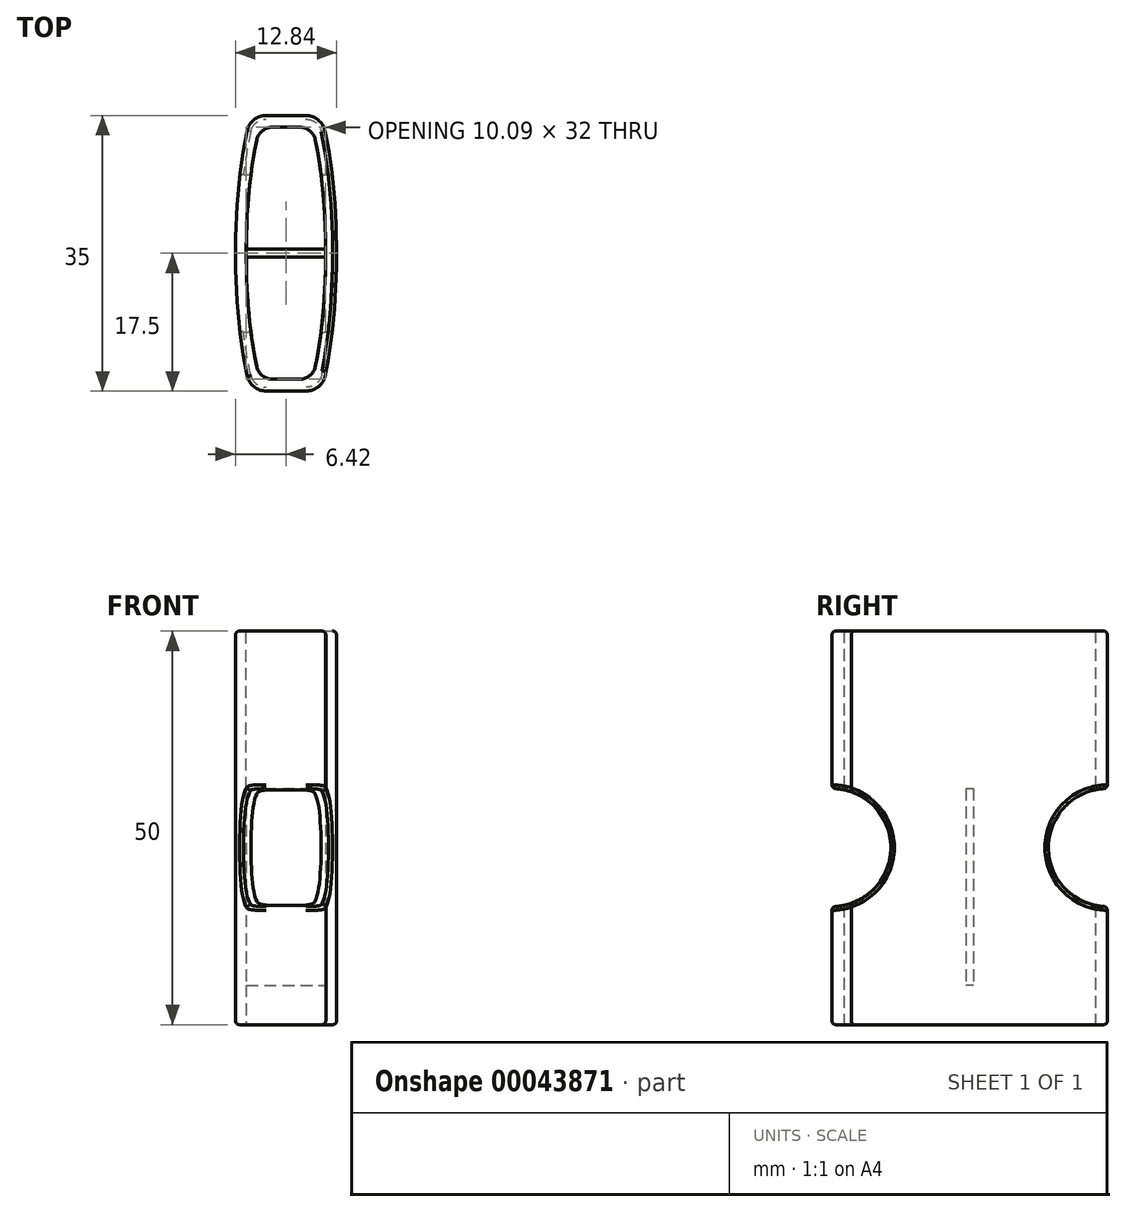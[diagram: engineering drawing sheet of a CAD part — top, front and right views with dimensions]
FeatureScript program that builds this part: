
annotation { "Feature Type Name" : "Feature", "Feature Type Description" : "" }
export const myFeature = defineFeature(function(context is Context, id is Id, definition is map)
    precondition{}
    {
        {
            var Q0;
            Q0=qCreatedBy(makeId("Top.planeOp"),FACE);
            var sketch = newSketch(context, id + "F0", { "sketchPlane" : qUnion([Q0])});
            skLineSegment(sketch, "E0.rect.bottom", {"start": v(-2.5, 17.5) * mm, "end": v(2.5, 17.5) * mm});
            skLineSegment(sketch, "E0.rect.top", {"start": v(-2.5, -17.5) * mm, "end": v(2.56, -17.5) * mm});
            skPoint(sketch, "E0.rect.middle", {"position": v(0, 0) * mm});
            skArc(sketch, "E1.filletArc", {"start": v(-4.06, -16.95) * mm, "mid": v(-3.33, -17.36) * mm, "end": v(-2.5, -17.5) * mm});
            skArc(sketch, "E2.filletArc", {"start": v(-4.94, -15.53) * mm, "mid": v(-4.62, -16.32) * mm, "end": v(-4.06, -16.95) * mm});
            skArc(sketch, "E3.filletArc", {"start": v(-2.5, 17.5) * mm, "mid": v(-4.07, 16.95) * mm, "end": v(-4.94, 15.53) * mm});
            skArc(sketch, "E4.filletArc", {"start": v(2.56, -17.5) * mm, "mid": v(4.33, -16.76) * mm, "end": v(5.06, -15) * mm});
            skArc(sketch, "E5.filletArc", {"start": v(4.94, 15.53) * mm, "mid": v(4.07, 16.95) * mm, "end": v(2.5, 17.5) * mm});
            skEllipticalArc(sketch, "E6", {});
            skEllipticalArc(sketch, "E7.trimOffspring", {});
            const initialGuessF0  = {"E6": [0, 0, 1, 0, 0.006417609448810679, 0.02435162757841252, 5.62005198816915, 0.6917273400470441], "E7.trimOffspring": [0, 0, 1, 0, 0.006417609448810679, 0.02435162757841252, 2.449865313542748, 3.8333199936368376]};
            skSetInitialGuess(sketch, initialGuessF0);
            skSolve(sketch);
        }
        {
            var Q0;
            Q0 = qSketchRegion(id + "F0", true);
            extrude(context, id + "F1", {"entities" : qUnion([Q0]), "depth" : 50 * mm});
        }
        {
            var Q0;
            Q0=makeQuery(id+"F1.opExtrude","CAP_FACE",FACE,{"disambiguationData":[OSD([sQuery(id+"F0.wireOp",EDGE,"E0.rect.bottom"),sQuery(id+"F0.wireOp",EDGE,"E0.rect.top"),sQuery(id+"F0.wireOp",EDGE,"E1.filletArc"),sQuery(id+"F0.wireOp",EDGE,"E2.filletArc"),sQuery(id+"F0.wireOp",EDGE,"E3.filletArc"),sQuery(id+"F0.wireOp",EDGE,"E4.filletArc"),sQuery(id+"F0.wireOp",EDGE,"E5.filletArc"),sQuery(id+"F0.wireOp",EDGE,"E6"),sQuery(id+"F0.wireOp",EDGE,"E7.trimOffspring")])],"isStart":true});
            var sketch = newSketch(context, id + "F2", { "sketchPlane" : qUnion([Q0])});
            skLineSegment(sketch, "E8.rect.bottom", {"start": v(1.76, 16) * mm, "end": v(-1.76, 16) * mm});
            skLineSegment(sketch, "E8.rect.top", {"start": v(1.76, -16) * mm, "end": v(-1.76, -16) * mm});
            skPoint(sketch, "E8.rect.middle", {"position": v(0, 0) * mm});
            skArc(sketch, "E9.filletArc", {"start": v(-3.7, -14.43) * mm, "mid": v(-3, -15.56) * mm, "end": v(-1.76, -16) * mm});
            skArc(sketch, "E10.filletArc", {"start": v(1.76, -16) * mm, "mid": v(3, -15.56) * mm, "end": v(3.7, -14.43) * mm});
            skArc(sketch, "E11.filletArc", {"start": v(-1.76, 16) * mm, "mid": v(-3, 15.56) * mm, "end": v(-3.7, 14.43) * mm});
            skArc(sketch, "E12.filletArc", {"start": v(3.7, 14.43) * mm, "mid": v(3, 15.56) * mm, "end": v(1.76, 16) * mm});
            skEllipticalArc(sketch, "E13", {});
            skEllipticalArc(sketch, "E14.trimOffspring", {});
            const initialGuessF2  = {"E13": [0, 0, 1, 0, 0.00504706840610105, 0.021278346083851495, 5.53809766870892, 0.7450876384706664], "E14.trimOffspring": [0, 0, 1, 0, 0.00504706840610105, 0.021278346083851495, 2.3965050151191267, 3.886680292060459]};
            skSetInitialGuess(sketch, initialGuessF2);
            skSolve(sketch);
        }
        {
            var Q0;
            Q0 = qSketchRegion(id + "F2", true);
            extrude(context, id + "F3", {"entities" : qUnion([Q0]), "operationType" : NewBodyOperationType.REMOVE, "endBound" : BoundingType.UP_TO_NEXT, "oppositeDirection" : true, "depth" : 25 * mm});
        }
        {
            var Q0;
            Q0=makeQuery(id+"F6.boolean.opBoolean","MERGE",FACE,{"derivedFrom":[makeQuery(id+"F1.opExtrude","CAP_FACE",FACE,{"disambiguationData":[OSD([sQuery(id+"F0.wireOp",EDGE,"E0.rect.bottom"),sQuery(id+"F0.wireOp",EDGE,"E0.rect.top"),sQuery(id+"F0.wireOp",EDGE,"E1.filletArc"),sQuery(id+"F0.wireOp",EDGE,"E2.filletArc"),sQuery(id+"F0.wireOp",EDGE,"E3.filletArc"),sQuery(id+"F0.wireOp",EDGE,"E4.filletArc"),sQuery(id+"F0.wireOp",EDGE,"E5.filletArc"),sQuery(id+"F0.wireOp",EDGE,"E6"),sQuery(id+"F0.wireOp",EDGE,"E7.trimOffspring")])],"isStart":true}),makeQuery(id+"F6.opExtrude","CAP_FACE",FACE,{"disambiguationData":[OSD([sQuery(id+"F5.wireOp",EDGE,"E15.rect.bottom"),sQuery(id+"F5.wireOp",EDGE,"E15.rect.top"),sQuery(id+"F5.wireOp",EDGE,"E15.rect.left"),sQuery(id+"F5.wireOp",EDGE,"E15.rect.right")])],"isStart":true})]});
            cPlane(context, id + "F4", {"entities" : qUnion([Q0]), "cplaneType" : CPlaneType.OFFSET, "offset" : 5 * mm, "oppositeDirection" : true, "width" : 150 * mm, "height" : 150 * mm});
        }
        {
            var Q0;
            Q0=qCreatedBy(id+"F4.planeOp",FACE);
            var sketch = newSketch(context, id + "F5", { "sketchPlane" : qUnion([Q0])});
            skLineSegment(sketch, "E15.rect.bottom", {"start": v(-5.05, -0.5) * mm, "end": v(5.05, -0.5) * mm});
            skLineSegment(sketch, "E15.rect.top", {"start": v(-5.05, 0.5) * mm, "end": v(5.05, 0.5) * mm});
            skLineSegment(sketch, "E15.rect.left", {"start": v(-5.05, -0.5) * mm, "end": v(-5.05, 0.5) * mm});
            skLineSegment(sketch, "E15.rect.right", {"start": v(5.05, -0.5) * mm, "end": v(5.05, 0.5) * mm});
            skPoint(sketch, "E15.rect.middle", {"position": v(0, 0) * mm});
            skSolve(sketch);
        }
        {
            var Q0;
            Q0 = qSketchRegion(id + "F5", true);
            extrude(context, id + "F6", {"entities" : qUnion([Q0]), "operationType" : NewBodyOperationType.ADD, "oppositeDirection" : true, "depth" : 25 * mm});
        }
        {
            var Q0;
            Q0=qCreatedBy(makeId("Right.planeOp"),FACE);
            var sketch = newSketch(context, id + "F7", { "sketchPlane" : qUnion([Q0])});
            skCircle(sketch, "E16", {"center": v(-17.5, 22.5) * mm, "radius": 7.5 * mm});
            skCircle(sketch, "E17", {"center": v(17.5, 22.5) * mm, "radius": 7.5 * mm});
            skSolve(sketch);
        }
        {
            var Q0;
            Q0 = qSketchRegion(id + "F7", true);
            extrude(context, id + "F8", {"entities" : qUnion([Q0]), "operationType" : NewBodyOperationType.REMOVE, "endBound" : BoundingType.SYMMETRIC, "oppositeDirection" : true, "depth" : 25 * mm});
        }
        {
            var Q0;
            Q0=makeQuery(id+"F8.boolean.opBoolean","INTERSECT",EDGE,{"derivedFrom":[makeQuery(id+"F1.opExtrude","SWEPT_FACE",FACE,{"disambiguationData":[OSD([sQuery(id+"F0.wireOp",EDGE,"E6")])]}),makeQuery(id+"F8.opExtrude","SWEPT_FACE",FACE,{"disambiguationData":[OSD([sQuery(id+"F7.wireOp",EDGE,"E16")])]})]});
            var Q1;
            Q1=makeQuery(id+"F8.boolean.opBoolean","INTERSECT",EDGE,{"disambiguationData":[OD(1.0)],"derivedFrom":[makeQuery(id+"F1.opExtrude","SWEPT_FACE",FACE,{"disambiguationData":[OSD([sQuery(id+"F0.wireOp",EDGE,"E4.filletArc")])]}),makeQuery(id+"F8.opExtrude","SWEPT_FACE",FACE,{"disambiguationData":[OSD([sQuery(id+"F7.wireOp",EDGE,"E16")])]})]});
            var Q2;
            Q2=makeQuery(id+"F8.boolean.opBoolean","INTERSECT",EDGE,{"disambiguationData":[OD(1.0)],"derivedFrom":[makeQuery(id+"F1.opExtrude","SWEPT_FACE",FACE,{"disambiguationData":[OSD([sQuery(id+"F0.wireOp",EDGE,"E0.rect.top")])]}),makeQuery(id+"F8.opExtrude","SWEPT_FACE",FACE,{"disambiguationData":[OSD([sQuery(id+"F7.wireOp",EDGE,"E16")])]})]});
            var Q3;
            Q3=makeQuery(id+"F8.boolean.opBoolean","INTERSECT",EDGE,{"disambiguationData":[OD(1.0)],"derivedFrom":[makeQuery(id+"F1.opExtrude","SWEPT_FACE",FACE,{"disambiguationData":[OSD([sQuery(id+"F0.wireOp",EDGE,"E1.filletArc"),sQuery(id+"F0.wireOp",EDGE,"E2.filletArc")])]}),makeQuery(id+"F8.opExtrude","SWEPT_FACE",FACE,{"disambiguationData":[OSD([sQuery(id+"F7.wireOp",EDGE,"E16")])]})]});
            var Q4;
            {var subQ3=sQuery(id+"F0.wireOp",EDGE,"E7.trimOffspring");Q4=makeQuery(id+"F8.boolean.opBoolean","INTERSECT",EDGE,{"derivedFrom":[makeQuery(id+"FSptWl8DsKj5TSb_1.boolean.opBoolean","SPLIT",FACE,{"disambiguationData":[TD([makeQuery(id+"F2ueWIRuqyq2hN0_1.boolean.opBoolean","COPY",FACE,{"derivedFrom":makeQuery(id+"F2ueWIRuqyq2hN0_1.opExtrude","SWEPT_FACE",FACE,{"disambiguationData":[OSD([sQuery(id+"FgZf1C2zDax0cFX_1.wireOp",EDGE,"f9be329c-f042-4575-97ac-8e7fd8f5c0c4.rect.top")])]})})])],"derivedFrom":makeQuery(id+"F1.opExtrude","SWEPT_FACE",FACE,{"disambiguationData":[OSD([subQ3])]})}),makeQuery(id+"F8.opExtrude","SWEPT_FACE",FACE,{"disambiguationData":[OSD([sQuery(id+"F7.wireOp",EDGE,"E16")])]})]});}
            var Q5;
            Q5=makeQuery(id+"F8.boolean.opBoolean","INTERSECT",EDGE,{"disambiguationData":[OD(0.0)],"derivedFrom":[makeQuery(id+"F1.opExtrude","SWEPT_FACE",FACE,{"disambiguationData":[OSD([sQuery(id+"F0.wireOp",EDGE,"E1.filletArc"),sQuery(id+"F0.wireOp",EDGE,"E2.filletArc")])]}),makeQuery(id+"F8.opExtrude","SWEPT_FACE",FACE,{"disambiguationData":[OSD([sQuery(id+"F7.wireOp",EDGE,"E16")])]})]});
            var Q6;
            Q6=makeQuery(id+"F8.boolean.opBoolean","INTERSECT",EDGE,{"disambiguationData":[OD(0.0)],"derivedFrom":[makeQuery(id+"F1.opExtrude","SWEPT_FACE",FACE,{"disambiguationData":[OSD([sQuery(id+"F0.wireOp",EDGE,"E0.rect.top")])]}),makeQuery(id+"F8.opExtrude","SWEPT_FACE",FACE,{"disambiguationData":[OSD([sQuery(id+"F7.wireOp",EDGE,"E16")])]})]});
            var Q7;
            Q7=makeQuery(id+"F8.boolean.opBoolean","INTERSECT",EDGE,{"disambiguationData":[OD(0.0)],"derivedFrom":[makeQuery(id+"F1.opExtrude","SWEPT_FACE",FACE,{"disambiguationData":[OSD([sQuery(id+"F0.wireOp",EDGE,"E4.filletArc")])]}),makeQuery(id+"F8.opExtrude","SWEPT_FACE",FACE,{"disambiguationData":[OSD([sQuery(id+"F7.wireOp",EDGE,"E16")])]})]});
            var Q8;
            Q8=makeQuery(id+"F1.opExtrude","CAP_EDGE",EDGE,{"disambiguationData":[OSD([sQuery(id+"F0.wireOp",EDGE,"E6")])],"isStart":true});
            var Q9;
            Q9=makeQuery(id+"F1.opExtrude","CAP_EDGE",EDGE,{"disambiguationData":[OSD([sQuery(id+"F0.wireOp",EDGE,"E4.filletArc")])],"isStart":true});
            var Q10;
            Q10=makeQuery(id+"F8.boolean.opBoolean","INTERSECT",EDGE,{"derivedFrom":[makeQuery(id+"F1.opExtrude","SWEPT_FACE",FACE,{"disambiguationData":[OSD([sQuery(id+"F0.wireOp",EDGE,"E6")])]}),makeQuery(id+"F8.opExtrude","SWEPT_FACE",FACE,{"disambiguationData":[OSD([sQuery(id+"F7.wireOp",EDGE,"E17")])]})]});
            var Q11;
            Q11=makeQuery(id+"F2ueWIRuqyq2hN0_1.boolean.opBoolean","INTERSECT",EDGE,{"derivedFrom":[makeQuery(id+"F1.opExtrude","SWEPT_FACE",FACE,{"disambiguationData":[OSD([sQuery(id+"F0.wireOp",EDGE,"E6")])]}),makeQuery(id+"F2ueWIRuqyq2hN0_1.opExtrude","SWEPT_FACE",FACE,{"disambiguationData":[OSD([sQuery(id+"FgZf1C2zDax0cFX_1.wireOp",EDGE,"f9be329c-f042-4575-97ac-8e7fd8f5c0c4.rect.top")])]})]});
            var Q12;
            Q12=makeQuery(id+"F2ueWIRuqyq2hN0_1.boolean.opBoolean","INTERSECT",EDGE,{"derivedFrom":[makeQuery(id+"F1.opExtrude","SWEPT_FACE",FACE,{"disambiguationData":[OSD([sQuery(id+"F0.wireOp",EDGE,"E4.filletArc")])]}),makeQuery(id+"F2ueWIRuqyq2hN0_1.opExtrude","SWEPT_FACE",FACE,{"disambiguationData":[OSD([sQuery(id+"FgZf1C2zDax0cFX_1.wireOp",EDGE,"f9be329c-f042-4575-97ac-8e7fd8f5c0c4.rect.right")])]})]});
            var Q13;
            Q13=makeQuery(id+"F2ueWIRuqyq2hN0_1.boolean.opBoolean","INTERSECT",EDGE,{"derivedFrom":[makeQuery(id+"F1.opExtrude","CAP_FACE",FACE,{"disambiguationData":[OSD([sQuery(id+"F0.wireOp",EDGE,"E0.rect.bottom"),sQuery(id+"F0.wireOp",EDGE,"E0.rect.top"),sQuery(id+"F0.wireOp",EDGE,"E1.filletArc"),sQuery(id+"F0.wireOp",EDGE,"E2.filletArc"),sQuery(id+"F0.wireOp",EDGE,"E3.filletArc"),sQuery(id+"F0.wireOp",EDGE,"E4.filletArc"),sQuery(id+"F0.wireOp",EDGE,"E5.filletArc"),sQuery(id+"F0.wireOp",EDGE,"E6"),sQuery(id+"F0.wireOp",EDGE,"E7.trimOffspring")])],"isStart":false}),makeQuery(id+"F2ueWIRuqyq2hN0_1.opExtrude","CAP_FACE",FACE,{"disambiguationData":[OSD([sQuery(id+"FgZf1C2zDax0cFX_1.wireOp",EDGE,"f9be329c-f042-4575-97ac-8e7fd8f5c0c4.rect.bottom"),sQuery(id+"FgZf1C2zDax0cFX_1.wireOp",EDGE,"f9be329c-f042-4575-97ac-8e7fd8f5c0c4.rect.top"),sQuery(id+"FgZf1C2zDax0cFX_1.wireOp",EDGE,"f9be329c-f042-4575-97ac-8e7fd8f5c0c4.rect.left"),sQuery(id+"FgZf1C2zDax0cFX_1.wireOp",EDGE,"f9be329c-f042-4575-97ac-8e7fd8f5c0c4.rect.right"),sQuery(id+"FgZf1C2zDax0cFX_1.wireOp",EDGE,"16942fb4-0f93-41b3-9ee7-52be9d19c08b.filletArc"),sQuery(id+"FgZf1C2zDax0cFX_1.wireOp",EDGE,"4a0630b5-12f0-4528-a6d2-bdece72b8eb2.filletArc")])],"isStart":true})]});
            var Q14;
            Q14=makeQuery(id+"F2ueWIRuqyq2hN0_1.boolean.opBoolean","INTERSECT",EDGE,{"derivedFrom":[makeQuery(id+"F1.opExtrude","CAP_FACE",FACE,{"disambiguationData":[OSD([sQuery(id+"F0.wireOp",EDGE,"E0.rect.bottom"),sQuery(id+"F0.wireOp",EDGE,"E0.rect.top"),sQuery(id+"F0.wireOp",EDGE,"E1.filletArc"),sQuery(id+"F0.wireOp",EDGE,"E2.filletArc"),sQuery(id+"F0.wireOp",EDGE,"E3.filletArc"),sQuery(id+"F0.wireOp",EDGE,"E4.filletArc"),sQuery(id+"F0.wireOp",EDGE,"E5.filletArc"),sQuery(id+"F0.wireOp",EDGE,"E6"),sQuery(id+"F0.wireOp",EDGE,"E7.trimOffspring")])],"isStart":false}),makeQuery(id+"F2ueWIRuqyq2hN0_1.opExtrude","SWEPT_FACE",FACE,{"disambiguationData":[OSD([sQuery(id+"FgZf1C2zDax0cFX_1.wireOp",EDGE,"f9be329c-f042-4575-97ac-8e7fd8f5c0c4.rect.left")])]})]});
            var Q15;
            Q15=makeQuery(id+"F2ueWIRuqyq2hN0_1.boolean.opBoolean","INTERSECT",EDGE,{"derivedFrom":[makeQuery(id+"F1.opExtrude","CAP_FACE",FACE,{"disambiguationData":[OSD([sQuery(id+"F0.wireOp",EDGE,"E0.rect.bottom"),sQuery(id+"F0.wireOp",EDGE,"E0.rect.top"),sQuery(id+"F0.wireOp",EDGE,"E1.filletArc"),sQuery(id+"F0.wireOp",EDGE,"E2.filletArc"),sQuery(id+"F0.wireOp",EDGE,"E3.filletArc"),sQuery(id+"F0.wireOp",EDGE,"E4.filletArc"),sQuery(id+"F0.wireOp",EDGE,"E5.filletArc"),sQuery(id+"F0.wireOp",EDGE,"E6"),sQuery(id+"F0.wireOp",EDGE,"E7.trimOffspring")])],"isStart":false}),makeQuery(id+"F2ueWIRuqyq2hN0_1.opExtrude","SWEPT_FACE",FACE,{"disambiguationData":[OSD([sQuery(id+"FgZf1C2zDax0cFX_1.wireOp",EDGE,"f9be329c-f042-4575-97ac-8e7fd8f5c0c4.rect.right")])]})]});
            var Q16;
            Q16=makeQuery(id+"F1.opExtrude","CAP_EDGE",EDGE,{"disambiguationData":[OSD([sQuery(id+"F0.wireOp",EDGE,"E7.trimOffspring")])],"isStart":false});
            fillet(context, id + "F9", {"entities" : qUnion([Q0, Q1, Q2, Q3, Q4, Q5, Q6, Q7, Q8, Q9, Q10, Q11, Q12, Q13, Q14, Q15, Q16]), "radius" : 0.5 * mm, "tangentPropagation" : true, "allowEdgeOverflow" : false});
        }
    });
